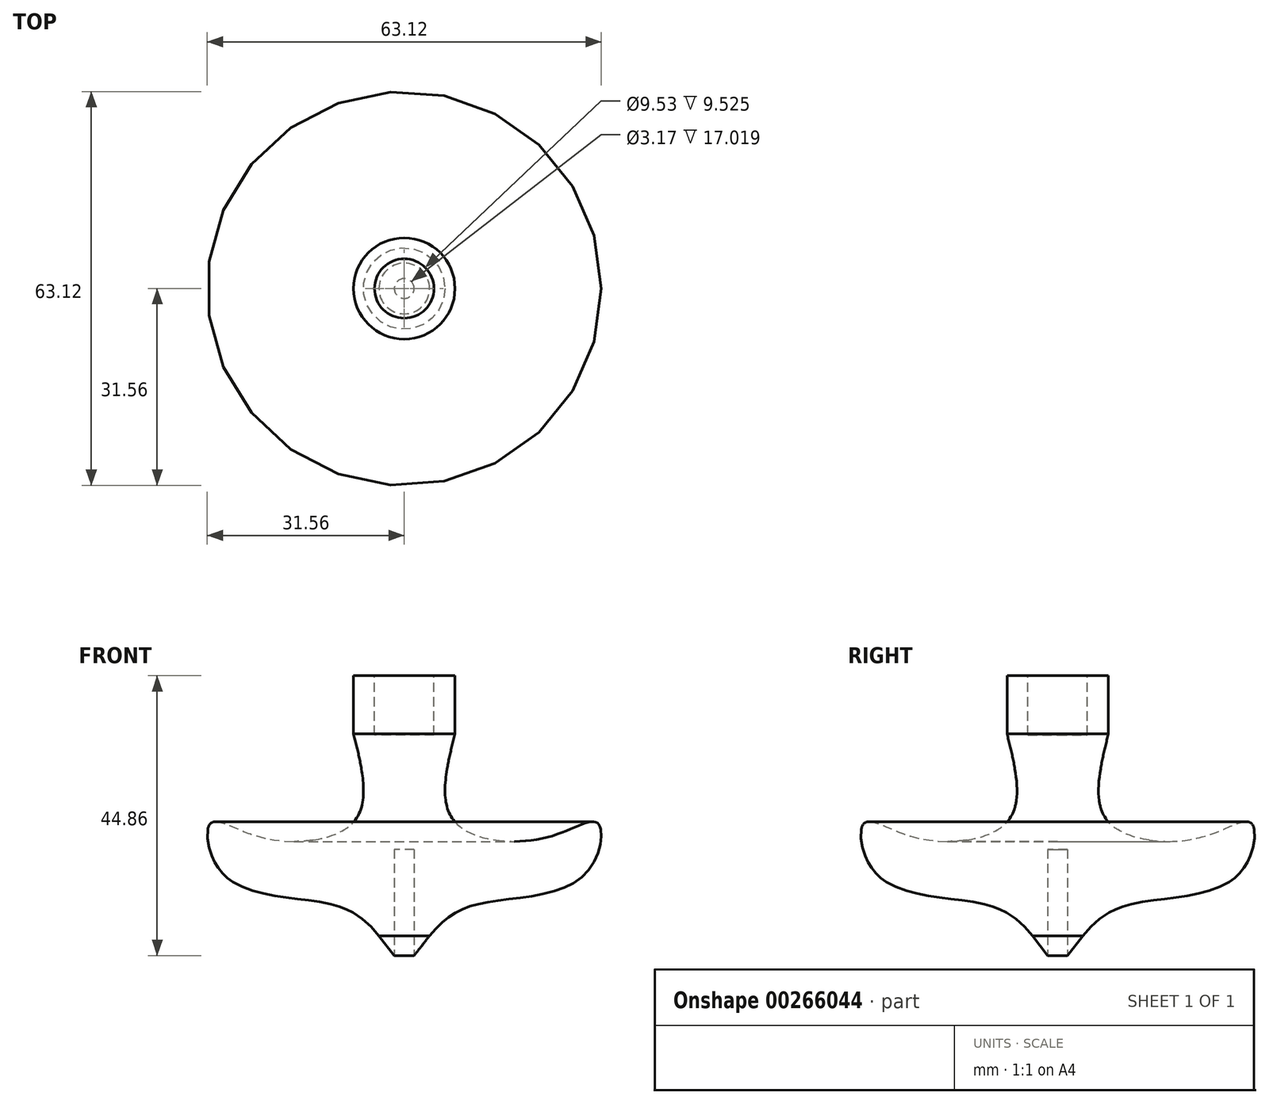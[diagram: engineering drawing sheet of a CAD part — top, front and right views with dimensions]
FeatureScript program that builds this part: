
annotation { "Feature Type Name" : "Feature", "Feature Type Description" : "" }
export const myFeature = defineFeature(function(context is Context, id is Id, definition is map)
    precondition{}
    {
        {
            var Q0;
            Q0=qCreatedBy(makeId("Front.planeOp"),FACE);
            var sketch = newSketch(context, id + "F0", { "sketchPlane" : qUnion([Q0])});
            skLineSegment(sketch, "E0", {"start": v(0, 0) * mm, "end": v(0, 46.9) * mm});
            skLineSegment(sketch, "E1", {"start": v(0, 46.9) * mm, "end": v(8.12, 46.9) * mm});
            skLineSegment(sketch, "E2", {"start": v(8.12, 46.9) * mm, "end": v(8.12, 37.56) * mm});
            skLineSegment(sketch, "E3", {"start": v(0, 0) * mm, "end": v(4.06, 5.2) * mm});
            skPoint(sketch, "E3.endSnap0", {"position": v(4.06, 46.9) * mm});
            skLineSegment(sketch, "E4.left", {"start": v(0, 46.9) * mm, "end": v(0, 0) * mm});
            skPoint(sketch, "E5", {"position": v(31.02, 23.2) * mm});
            skPoint(sketch, "E6", {"position": v(0, 23.45) * mm});
            skPoint(sketch, "E7", {"position": v(23.09, 21.02) * mm});
            skPoint(sketch, "E8", {"position": v(28.86, 14.96) * mm});
            skPoint(sketch, "E9", {"position": v(12.8, 10.49) * mm});
            skFitSpline(sketch, "E10", {"points": [v(8.12, 37.56) * mm, v(8.12, 23.45) * mm, v(23.09, 21.02) * mm, v(31.02, 23.2) * mm, v(28.86, 14.96) * mm, v(12.8, 10.49) * mm, v(4.06, 5.2) * mm], "startDerivative": vector(-24.4, -96.3) * mm, "endDerivative": vector(-50.13, -61.18) * mm});
            skPoint(sketch, "E11", {"position": v(13.33, 32.47) * mm});
            skPoint(sketch, "E12", {"position": v(13.33, 24.93) * mm});
            skFitSpline(sketch, "E13", {"points": [v(6.64, 31.74) * mm, v(13.33, 32.47) * mm, v(13.33, 24.93) * mm, v(8.12, 23.45) * mm], "startDerivative": vector(28.55, 27.55) * mm, "endDerivative": vector(-6.45, -9.86) * mm});
            skPoint(sketch, "E14", {"position": v(0, 9.46) * mm});
            skArc(sketch, "E15", {"start": v(31.48, 22.23) * mm, "mid": v(22.24, 29.46) * mm, "end": v(14.62, 20.53) * mm});
            skFitSpline(sketch, "E16.trimOffspring", {"points": [v(8.12, 37.56) * mm, v(8.12, 23.45) * mm, v(23.09, 21.02) * mm, v(31.02, 23.2) * mm, v(28.86, 14.96) * mm, v(12.8, 10.49) * mm, v(4.06, 5.2) * mm], "startDerivative": vector(-24.4, -96.3) * mm, "endDerivative": vector(-50.13, -61.18) * mm});
            skPoint(sketch, "E17", {"position": v(31.48, 46.9) * mm});
            skPoint(sketch, "E18", {"position": v(1.5, 1.92) * mm});
            skSolve(sketch);
        }
        {
            var Q0;
            Q0=makeQuery(id+"F0.imprint","IMPRINT",FACE,{"disambiguationData":[TD([[makeQuery(id+"F0.imprint","IMPRINT",EDGE,{"derivedFrom":sQuery(id+"F0.wireOp",EDGE,"E1")}),-1.0]])]});
            var Q1;
            Q1=sQuery(id+"F0.wireOp",EDGE,"E4.left");
            revolve(context, id + "F1", {"entities" : qUnion([Q0]), "axis" : qUnion([Q1]), "revolveType" : RevolveType.FULL});
        }
        {
            var Q0;
            Q0=makeQuery(id+"F1.opRevolve","SWEPT_FACE",FACE,{"disambiguationData":[OSD([sQuery(id+"F0.wireOp",EDGE,"E1")])]});
            var sketch = newSketch(context, id + "F2", { "sketchPlane" : qUnion([Q0])});
            skCircle(sketch, "E19", {"center": v(0, 0) * mm, "radius": 4.76 * mm});
            skSolve(sketch);
        }
        {
            var Q0;
            Q0 = qSketchRegion(id + "F2", true);
            extrude(context, id + "F3", {"entities" : qUnion([Q0]), "operationType" : NewBodyOperationType.REMOVE, "oppositeDirection" : true, "depth" : 9.52 * mm});
        }
        {
            var Q0;
            Q0=qCreatedBy(makeId("Top.planeOp"),FACE);
            var sketch = newSketch(context, id + "F4", { "sketchPlane" : qUnion([Q0])});
            skCircle(sketch, "E20", {"center": v(0, 0) * mm, "radius": 1.58 * mm});
            skSolve(sketch);
        }
        {
            var Q0;
            Q0 = qSketchRegion(id + "F4", true);
            extrude(context, id + "F5", {"entities" : qUnion([Q0]), "operationType" : NewBodyOperationType.REMOVE, "depth" : 19.05 * mm});
        }
    });
